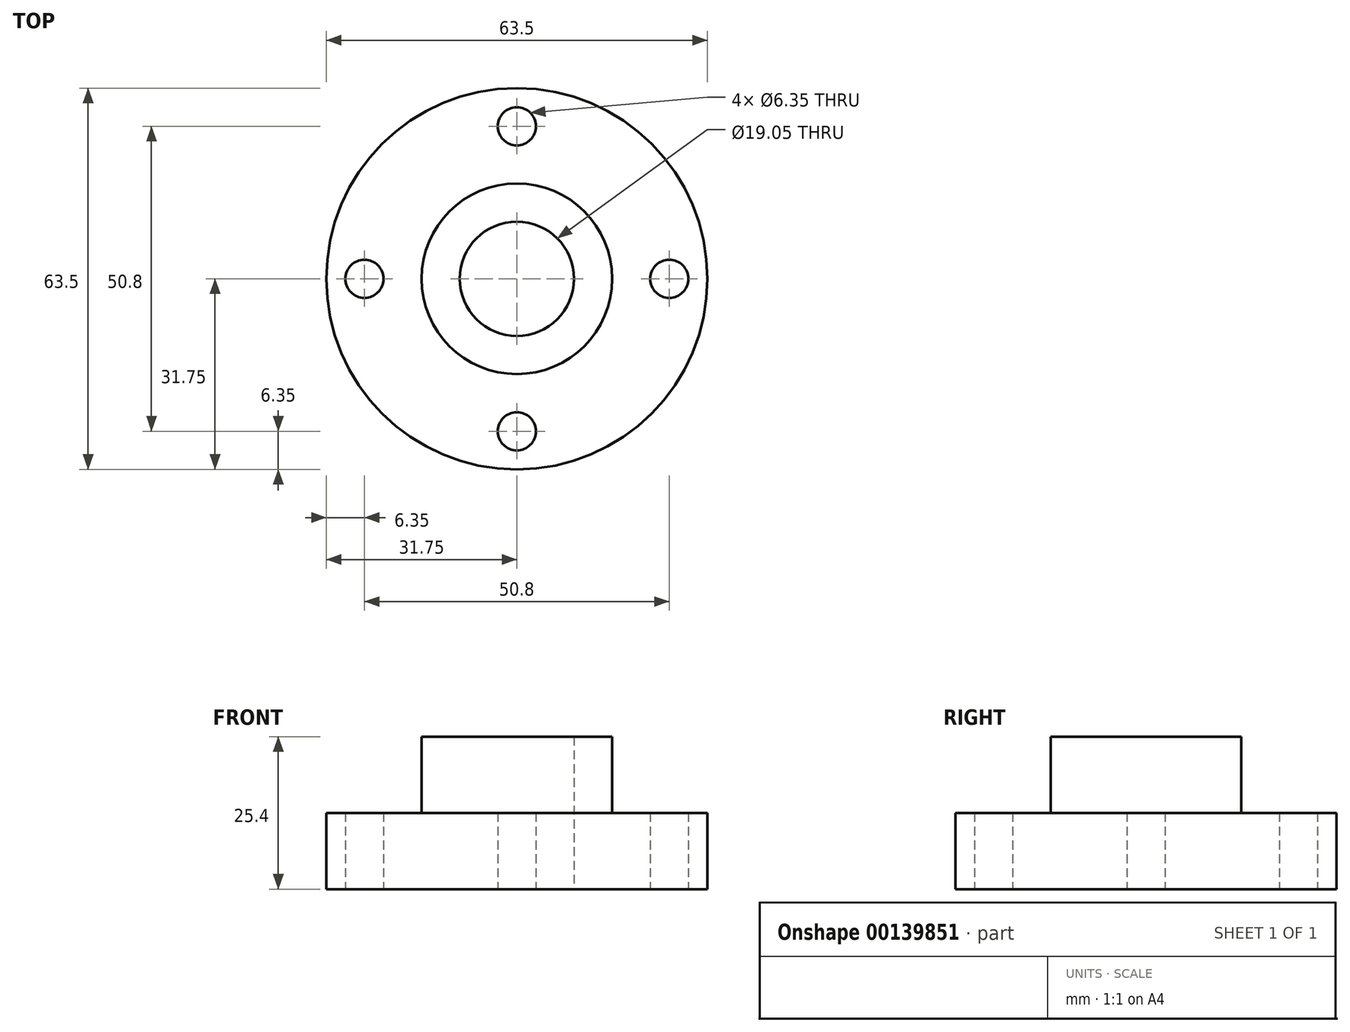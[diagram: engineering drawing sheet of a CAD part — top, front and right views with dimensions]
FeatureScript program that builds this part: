
annotation { "Feature Type Name" : "Feature", "Feature Type Description" : "" }
export const myFeature = defineFeature(function(context is Context, id is Id, definition is map)
    precondition{}
    {
        {
            var Q0;
            Q0=qCreatedBy(makeId("Top.planeOp"),FACE);
            var sketch = newSketch(context, id + "F0", { "sketchPlane" : qUnion([Q0])});
            skCircle(sketch, "E0", {"center": v(0, 0) * mm, "radius": 9.53 * mm});
            skCircle(sketch, "E1", {"center": v(0, 0) * mm, "radius": 15.88 * mm});
            skSolve(sketch);
        }
        {
            var Q0;
            Q0 = qSketchRegion(id + "F0", true);
            extrude(context, id + "F1", {"entities" : qUnion([Q0]), "depth" : 25.4 * mm});
        }
        {
            var Q0;
            Q0=qCreatedBy(makeId("Top.planeOp"),FACE);
            var sketch = newSketch(context, id + "F2", { "sketchPlane" : qUnion([Q0])});
            skCircle(sketch, "E2", {"center": v(0, 0) * mm, "radius": 15.88 * mm});
            skCircle(sketch, "E3", {"center": v(0, 0) * mm, "radius": 31.75 * mm});
            skSolve(sketch);
        }
        {
            var Q0;
            Q0 = qSketchRegion(id + "F2", true);
            extrude(context, id + "F3", {"entities" : qUnion([Q0]), "operationType" : NewBodyOperationType.ADD, "depth" : 12.7 * mm});
        }
        {
            var Q0;
            Q0=qCreatedBy(makeId("Top.planeOp"),FACE);
            var sketch = newSketch(context, id + "F4", { "sketchPlane" : qUnion([Q0])});
            skCircle(sketch, "E4", {"center": v(0, 0) * mm, "radius": 25.4 * mm});
            skCircle(sketch, "E5", {"center": v(0, -25.4) * mm, "radius": 3.18 * mm});
            skCircle(sketch, "E6.1.0", {"center": v(25.4, 0) * mm, "radius": 3.18 * mm});
            skCircle(sketch, "E6.2.0", {"center": v(0, 25.4) * mm, "radius": 3.18 * mm});
            skCircle(sketch, "E6.3.0", {"center": v(-25.4, 0) * mm, "radius": 3.18 * mm});
            skSolve(sketch);
        }
        {
            var Q0;
            {var subQ0=sQuery(id+"F4.wireOp",EDGE,"E5");var subQ1=sQuery(id+"F4.wireOp",EDGE,"E4");var subQ2=makeQuery(id+"F4.imprint","INTERSECT",VERTEX,{"disambiguationData":[OD(0.0)],"derivedFrom":[subQ1,subQ0]});Q0=makeQuery(id+"F4.imprint","IMPRINT",FACE,{"disambiguationData":[TD([[makeQuery(id+"F4.imprint","IMPRINT",EDGE,{"disambiguationData":[TD([[subQ2,-1.0]])],"derivedFrom":subQ1}),-1.0]])]});}
            var Q1;
            {var subQ0=sQuery(id+"F4.wireOp",EDGE,"E5");var subQ1=sQuery(id+"F4.wireOp",EDGE,"E4");var subQ2=makeQuery(id+"F4.imprint","INTERSECT",VERTEX,{"disambiguationData":[OD(0.0)],"derivedFrom":[subQ1,subQ0]});Q1=makeQuery(id+"F4.imprint","IMPRINT",FACE,{"disambiguationData":[TD([[makeQuery(id+"F4.imprint","IMPRINT",EDGE,{"disambiguationData":[TD([[subQ2,-1.0]])],"derivedFrom":subQ1}),1.0]])]});}
            var Q2;
            {var subQ0=sQuery(id+"F4.wireOp",EDGE,"E6.1.0");var subQ1=sQuery(id+"F4.wireOp",EDGE,"E4");var subQ2=makeQuery(id+"F4.imprint","INTERSECT",VERTEX,{"disambiguationData":[OD(0.0)],"derivedFrom":[subQ1,subQ0]});Q2=makeQuery(id+"F4.imprint","IMPRINT",FACE,{"disambiguationData":[TD([[makeQuery(id+"F4.imprint","IMPRINT",EDGE,{"disambiguationData":[TD([[subQ2,1.0]])],"derivedFrom":subQ1}),-1.0]])]});}
            var Q3;
            {var subQ0=sQuery(id+"F4.wireOp",EDGE,"E6.1.0");var subQ1=sQuery(id+"F4.wireOp",EDGE,"E4");var subQ2=makeQuery(id+"F4.imprint","INTERSECT",VERTEX,{"disambiguationData":[OD(0.0)],"derivedFrom":[subQ1,subQ0]});Q3=makeQuery(id+"F4.imprint","IMPRINT",FACE,{"disambiguationData":[TD([[makeQuery(id+"F4.imprint","IMPRINT",EDGE,{"disambiguationData":[TD([[subQ2,1.0]])],"derivedFrom":subQ1}),1.0]])]});}
            var Q4;
            {var subQ0=sQuery(id+"F4.wireOp",EDGE,"E6.2.0");var subQ1=sQuery(id+"F4.wireOp",EDGE,"E4");var subQ2=makeQuery(id+"F4.imprint","INTERSECT",VERTEX,{"disambiguationData":[OD(0.0)],"derivedFrom":[subQ1,subQ0]});Q4=makeQuery(id+"F4.imprint","IMPRINT",FACE,{"disambiguationData":[TD([[makeQuery(id+"F4.imprint","IMPRINT",EDGE,{"disambiguationData":[TD([[subQ2,-1.0]])],"derivedFrom":subQ1}),-1.0]])]});}
            var Q5;
            {var subQ0=sQuery(id+"F4.wireOp",EDGE,"E6.2.0");var subQ1=sQuery(id+"F4.wireOp",EDGE,"E4");var subQ2=makeQuery(id+"F4.imprint","INTERSECT",VERTEX,{"disambiguationData":[OD(0.0)],"derivedFrom":[subQ1,subQ0]});Q5=makeQuery(id+"F4.imprint","IMPRINT",FACE,{"disambiguationData":[TD([[makeQuery(id+"F4.imprint","IMPRINT",EDGE,{"disambiguationData":[TD([[subQ2,-1.0]])],"derivedFrom":subQ1}),1.0]])]});}
            var Q6;
            {var subQ0=sQuery(id+"F4.wireOp",EDGE,"E6.3.0");var subQ1=sQuery(id+"F4.wireOp",EDGE,"E4");var subQ2=makeQuery(id+"F4.imprint","INTERSECT",VERTEX,{"disambiguationData":[OD(0.0)],"derivedFrom":[subQ1,subQ0]});Q6=makeQuery(id+"F4.imprint","IMPRINT",FACE,{"disambiguationData":[TD([[makeQuery(id+"F4.imprint","IMPRINT",EDGE,{"disambiguationData":[TD([[subQ2,-1.0]])],"derivedFrom":subQ1}),-1.0]])]});}
            var Q7;
            {var subQ0=sQuery(id+"F4.wireOp",EDGE,"E6.3.0");var subQ1=sQuery(id+"F4.wireOp",EDGE,"E4");var subQ2=makeQuery(id+"F4.imprint","INTERSECT",VERTEX,{"disambiguationData":[OD(0.0)],"derivedFrom":[subQ1,subQ0]});Q7=makeQuery(id+"F4.imprint","IMPRINT",FACE,{"disambiguationData":[TD([[makeQuery(id+"F4.imprint","IMPRINT",EDGE,{"disambiguationData":[TD([[subQ2,-1.0]])],"derivedFrom":subQ1}),1.0]])]});}
            extrude(context, id + "F5", {"entities" : qUnion([Q0, Q1, Q2, Q3, Q4, Q5, Q6, Q7]), "operationType" : NewBodyOperationType.REMOVE, "endBound" : BoundingType.THROUGH_ALL, "depth" : 25.4 * mm});
        }
    });
